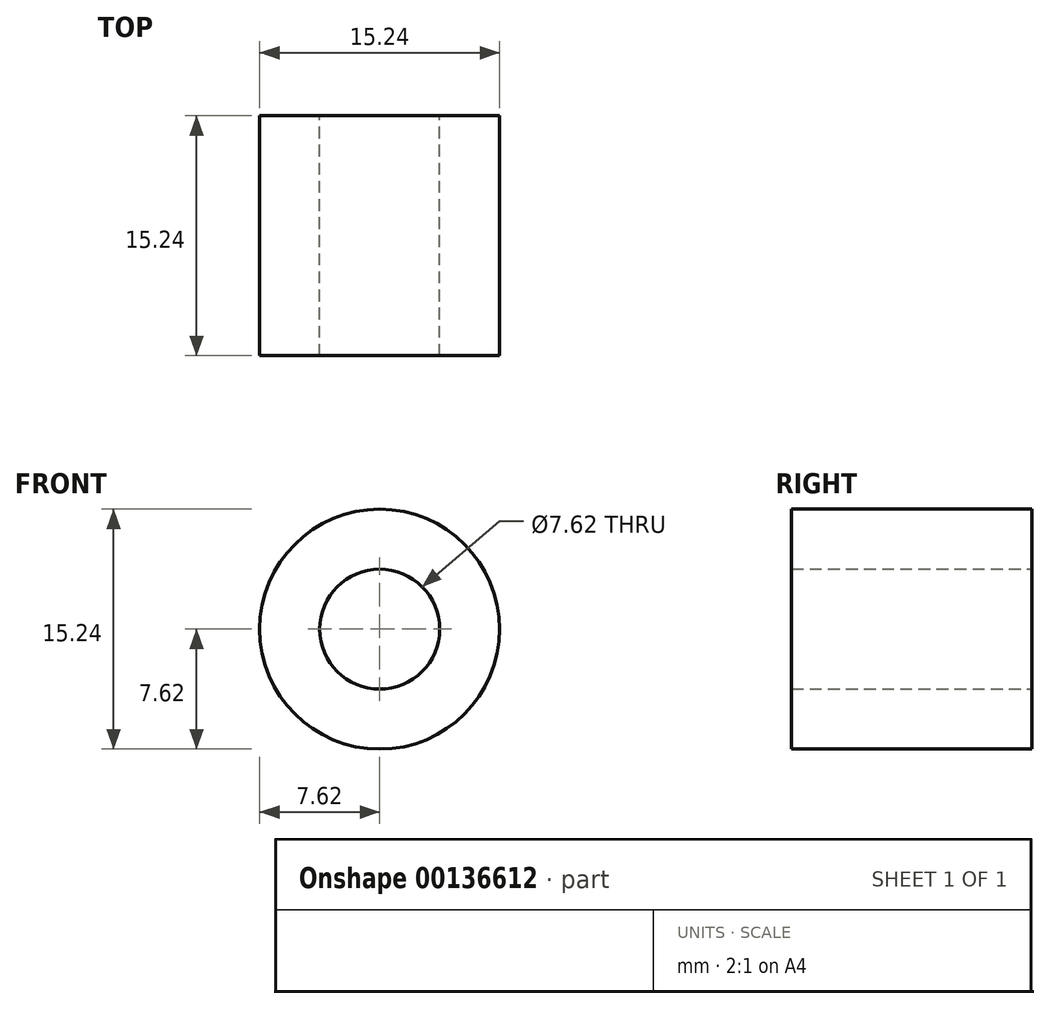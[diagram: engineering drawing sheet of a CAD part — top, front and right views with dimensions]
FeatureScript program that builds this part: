
annotation { "Feature Type Name" : "Feature", "Feature Type Description" : "" }
export const myFeature = defineFeature(function(context is Context, id is Id, definition is map)
    precondition{}
    {
        {
            var Q0;
            Q0=qCreatedBy(makeId("Front.planeOp"),FACE);
            var sketch = newSketch(context, id + "F0", { "sketchPlane" : qUnion([Q0])});
            skCircle(sketch, "E0", {"center": v(0, 0) * mm, "radius": 7.62 * mm});
            skCircle(sketch, "E1", {"center": v(0, 0) * mm, "radius": 3.81 * mm});
            skSolve(sketch);
        }
        {
            var Q0;
            Q0 = qSketchRegion(id + "F0", true);
            extrude(context, id + "F1", {"entities" : qUnion([Q0]), "depth" : 15.24 * mm});
        }
    });
